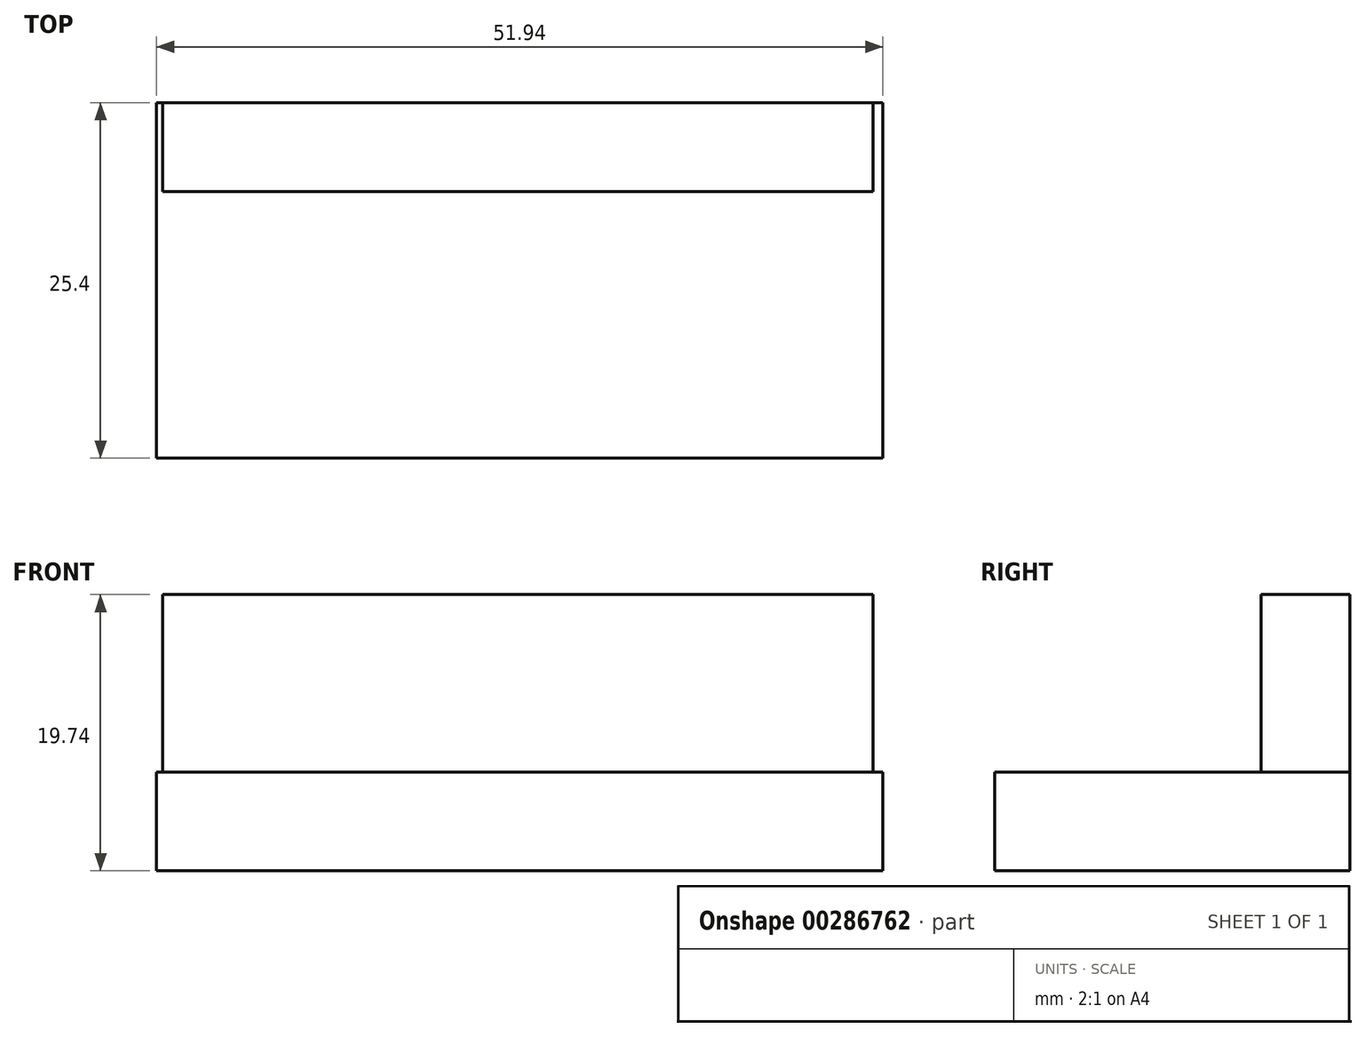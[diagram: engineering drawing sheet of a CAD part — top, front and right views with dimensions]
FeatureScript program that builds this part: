
annotation { "Feature Type Name" : "Feature", "Feature Type Description" : "" }
export const myFeature = defineFeature(function(context is Context, id is Id, definition is map)
    precondition{}
    {
        {
            var Q0;
            Q0=qCreatedBy(makeId("Front.planeOp"),FACE);
            var sketch = newSketch(context, id + "F0", { "sketchPlane" : qUnion([Q0])});
            skLineSegment(sketch, "E0", {"start": v(0, 0) * mm, "end": v(-25.4, 0) * mm});
            skLineSegment(sketch, "E1", {"start": v(0, 0) * mm, "end": v(25.4, 0) * mm});
            skLineSegment(sketch, "E2", {"start": v(25.4, 0) * mm, "end": v(25.4, 12.7) * mm});
            skLineSegment(sketch, "E3", {"start": v(-25.4, 0) * mm, "end": v(-25.4, 12.7) * mm});
            skLineSegment(sketch, "E4", {"start": v(-25.4, 12.7) * mm, "end": v(25.4, 12.7) * mm});
            skSolve(sketch);
        }
        {
            var Q0;
            Q0=makeQuery(id+"F0.imprint","IMPRINT",FACE,{"disambiguationData":[TD([[makeQuery(id+"F0.imprint","IMPRINT",EDGE,{"derivedFrom":sQuery(id+"F0.wireOp",EDGE,"E0")}),-1.0]])]});
            extrude(context, id + "F1", {"entities" : qUnion([Q0]), "depth" : 6.35 * mm});
        }
        {
            var Q0;
            Q0=qCreatedBy(makeId("Front.planeOp"),FACE);
            var sketch = newSketch(context, id + "F2", { "sketchPlane" : qUnion([Q0])});
            skLineSegment(sketch, "E5", {"start": v(26.1, 0) * mm, "end": v(0, 0) * mm});
            skLineSegment(sketch, "E6", {"start": v(0, 0) * mm, "end": v(-25.83, 0) * mm});
            skLineSegment(sketch, "E7", {"start": v(-25.83, 0) * mm, "end": v(-25.83, -7.04) * mm});
            skLineSegment(sketch, "E8", {"start": v(26.1, 0) * mm, "end": v(26.1, -7.04) * mm});
            skLineSegment(sketch, "E9", {"start": v(26.1, -7.04) * mm, "end": v(-25.83, -7.04) * mm});
            skSolve(sketch);
        }
        {
            var Q0;
            Q0 = qSketchRegion(id + "F2", true);
            extrude(context, id + "F3", {"entities" : qUnion([Q0]), "operationType" : NewBodyOperationType.ADD, "depth" : 25.4 * mm});
        }
        {
            var Q0;
            Q0 = qSketchRegion(id + "F2", true);
            extrude(context, id + "F4", {"entities" : qUnion([Q0]), "operationType" : NewBodyOperationType.ADD, "depth" : 25.4 * mm});
        }
    });
